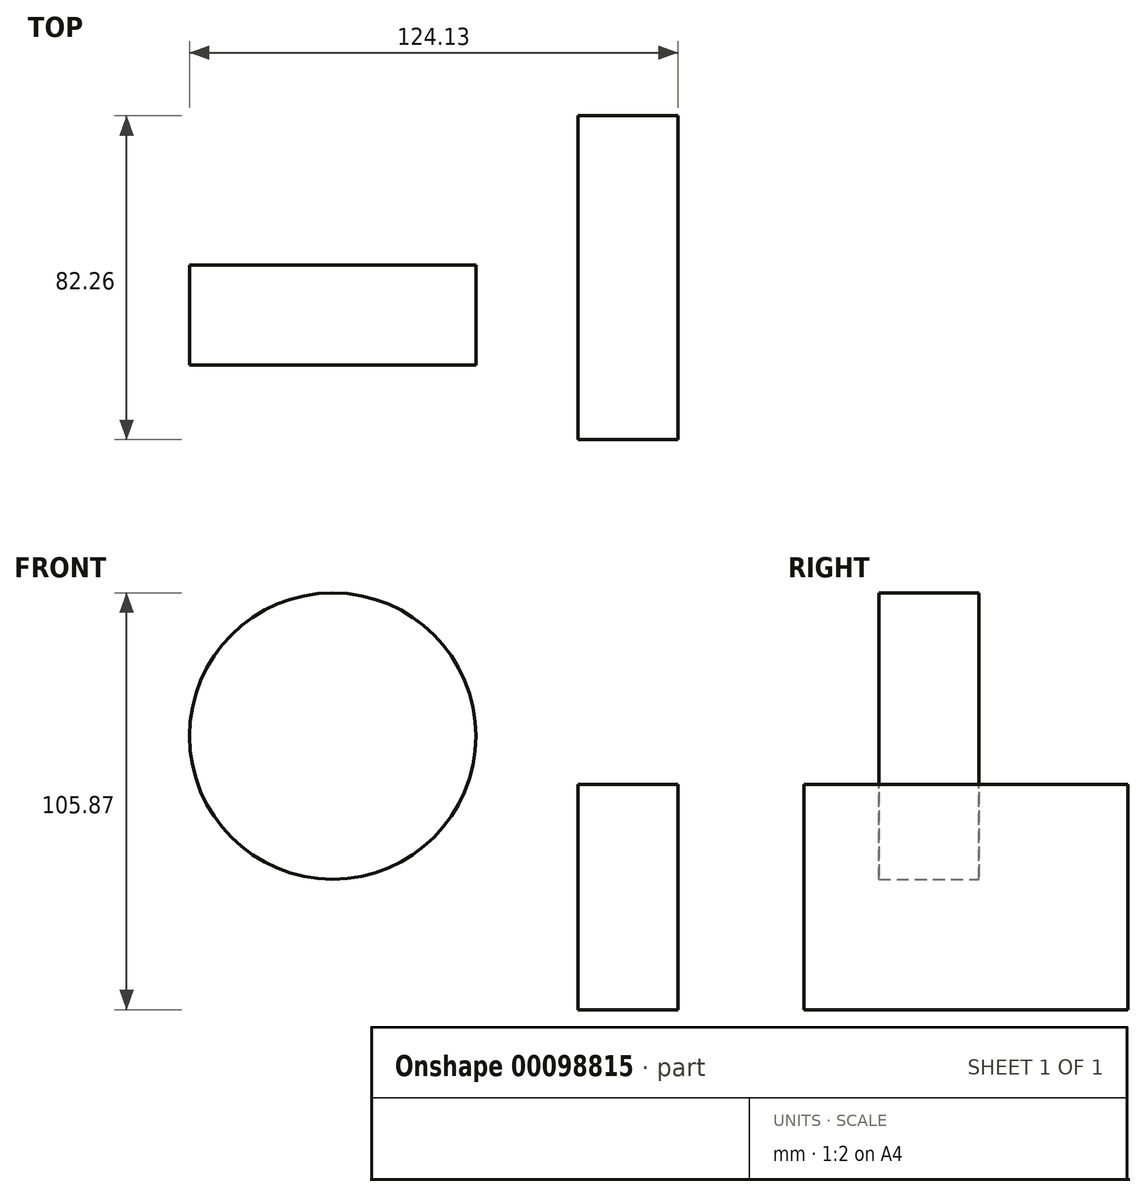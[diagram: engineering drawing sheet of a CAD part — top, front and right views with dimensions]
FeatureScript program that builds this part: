
annotation { "Feature Type Name" : "Feature", "Feature Type Description" : "" }
export const myFeature = defineFeature(function(context is Context, id is Id, definition is map)
    precondition{}
    {
        {
            var Q0;
            Q0=qCreatedBy(makeId("Right.planeOp"),FACE);
            var sketch = newSketch(context, id + "F0", { "sketchPlane" : qUnion([Q0])});
            skLineSegment(sketch, "E0.bottom", {"start": v(37.91, -13.8) * mm, "end": v(-44.35, -13.8) * mm});
            skLineSegment(sketch, "E0.top", {"start": v(37.91, 43.45) * mm, "end": v(-44.35, 43.45) * mm});
            skLineSegment(sketch, "E0.left", {"start": v(37.91, -13.8) * mm, "end": v(37.91, 43.45) * mm});
            skLineSegment(sketch, "E0.right", {"start": v(-44.35, -13.8) * mm, "end": v(-44.35, 43.45) * mm});
            skSolve(sketch);
        }
        {
            var Q0;
            Q0=makeQuery(id+"F0.imprint","IMPRINT",FACE,{"disambiguationData":[TD([[makeQuery(id+"F0.imprint","IMPRINT",EDGE,{"derivedFrom":sQuery(id+"F0.wireOp",EDGE,"E0.bottom")}),-1.0]])]});
            extrude(context, id + "F1", {"entities" : qUnion([Q0]), "depth" : 25.4 * mm});
        }
        {
            var Q0;
            Q0=qCreatedBy(makeId("Front.planeOp"),FACE);
            var sketch = newSketch(context, id + "F2", { "sketchPlane" : qUnion([Q0])});
            skCircle(sketch, "E1", {"center": v(-62.37, 55.72) * mm, "radius": 36.36 * mm});
            skSolve(sketch);
        }
        {
            var Q0;
            Q0=makeQuery(id+"F2.imprint","IMPRINT",FACE,{"disambiguationData":[TD([[makeQuery(id+"F2.imprint","IMPRINT",EDGE,{"derivedFrom":sQuery(id+"F2.wireOp",EDGE,"E1")}),1.0]])]});
            extrude(context, id + "F3", {"entities" : qUnion([Q0]), "depth" : 25.4 * mm});
        }
    });
